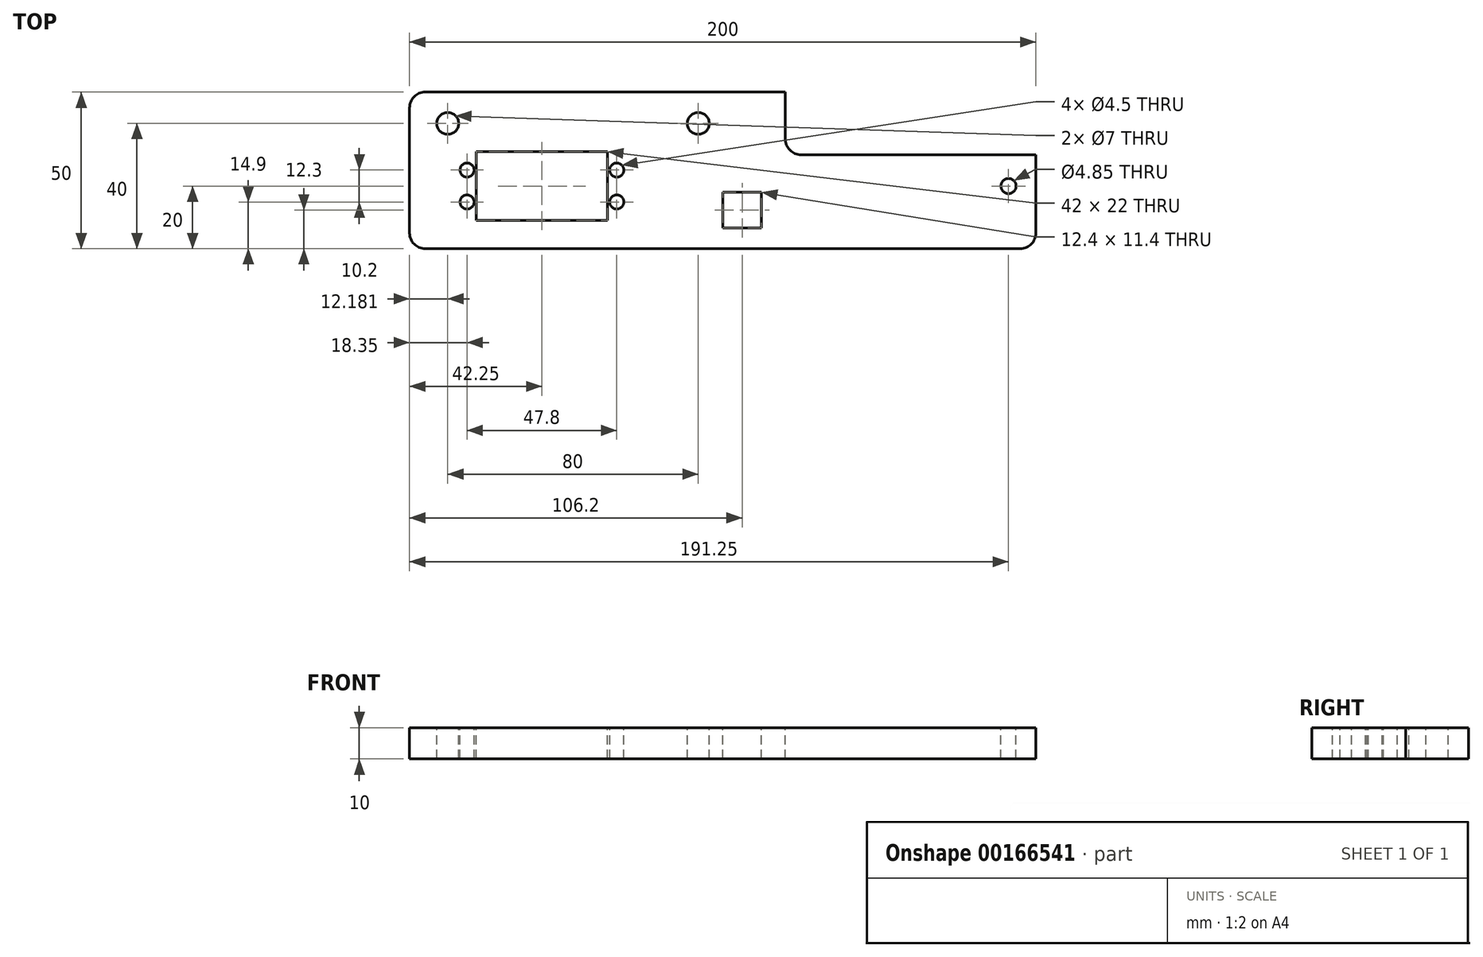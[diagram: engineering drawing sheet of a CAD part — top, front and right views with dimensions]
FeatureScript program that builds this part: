
annotation { "Feature Type Name" : "Feature", "Feature Type Description" : "" }
export const myFeature = defineFeature(function(context is Context, id is Id, definition is map)
    precondition{}
    {
        {
            var Q0;
            Q0=qCreatedBy(makeId("Top.planeOp"),FACE);
            var sketch = newSketch(context, id + "F0", { "sketchPlane" : qUnion([Q0])});
            skLineSegment(sketch, "E0.bottom", {"start": v(100, -25) * mm, "end": v(-100, -25) * mm});
            skLineSegment(sketch, "E0.top", {"start": v(100, 25) * mm, "end": v(-100, 25) * mm});
            skLineSegment(sketch, "E0.left", {"start": v(100, -25) * mm, "end": v(100, 25) * mm});
            skLineSegment(sketch, "E0.right", {"start": v(-100, -25) * mm, "end": v(-100, 25) * mm});
            skPoint(sketch, "E0.middle", {"position": v(0, 0) * mm});
            skSolve(sketch);
        }
        {
            var Q0;
            Q0=makeQuery(id+"F0.imprint","IMPRINT",FACE,{"disambiguationData":[TD([[makeQuery(id+"F0.imprint","IMPRINT",EDGE,{"derivedFrom":sQuery(id+"F0.wireOp",EDGE,"E0.bottom")}),-1.0]])]});
            extrude(context, id + "F1", {"entities" : qUnion([Q0]), "depth" : 10 * mm});
        }
        {
            var Q0;
            Q0=makeQuery(id+"F1.opExtrude","CAP_FACE",FACE,{"disambiguationData":[OSD([sQuery(id+"F0.wireOp",EDGE,"E0.bottom"),sQuery(id+"F0.wireOp",EDGE,"E0.top"),sQuery(id+"F0.wireOp",EDGE,"E0.left"),sQuery(id+"F0.wireOp",EDGE,"E0.right")])],"isStart":false});
            var sketch = newSketch(context, id + "F2", { "sketchPlane" : qUnion([Q0])});
            skLineSegment(sketch, "E1.bottom", {"start": v(-78.75, -16) * mm, "end": v(-36.75, -16) * mm});
            skLineSegment(sketch, "E1.top", {"start": v(-78.75, 6) * mm, "end": v(-36.75, 6) * mm});
            skLineSegment(sketch, "E1.left", {"start": v(-78.75, -16) * mm, "end": v(-78.75, 6) * mm});
            skLineSegment(sketch, "E1.right", {"start": v(-36.75, -16) * mm, "end": v(-36.75, 6) * mm});
            skPoint(sketch, "E1.middle", {"position": v(-57.75, -5) * mm});
            skSolve(sketch);
        }
        {
            var Q0;
            Q0=makeQuery(id+"F2.imprint","IMPRINT",FACE,{"disambiguationData":[TD([[makeQuery(id+"F2.imprint","IMPRINT",EDGE,{"derivedFrom":sQuery(id+"F2.wireOp",EDGE,"E1.bottom")}),1.0]])]});
            extrude(context, id + "F3", {"entities" : qUnion([Q0]), "operationType" : NewBodyOperationType.REMOVE, "endBound" : BoundingType.THROUGH_ALL, "oppositeDirection" : true, "depth" : 25 * mm});
        }
        {
            var Q0;
            Q0=makeQuery(id+"F1.opExtrude","CAP_FACE",FACE,{"disambiguationData":[OSD([sQuery(id+"F0.wireOp",EDGE,"E0.bottom"),sQuery(id+"F0.wireOp",EDGE,"E0.top"),sQuery(id+"F0.wireOp",EDGE,"E0.left"),sQuery(id+"F0.wireOp",EDGE,"E0.right")])],"isStart":false});
            var sketch = newSketch(context, id + "F4", { "sketchPlane" : qUnion([Q0])});
            skLineSegment(sketch, "E2.bottom", {"start": v(-81.65, 0.1) * mm, "end": v(-33.85, 0.1) * mm});
            skLineSegment(sketch, "E2.top", {"start": v(-81.65, -10.1) * mm, "end": v(-33.85, -10.1) * mm});
            skLineSegment(sketch, "E2.left", {"start": v(-81.65, 0.1) * mm, "end": v(-81.65, -10.1) * mm});
            skLineSegment(sketch, "E2.right", {"start": v(-33.85, 0.1) * mm, "end": v(-33.85, -10.1) * mm});
            skPoint(sketch, "E2.middle", {"position": v(-57.75, -5) * mm});
            skPoint(sketch, "E2.middle.positionSnap0", {"position": v(-78.75, -5) * mm});
            skPoint(sketch, "E2.middle.positionSnap1", {"position": v(-57.75, -16) * mm});
            skPoint(sketch, "E2.centerSnap0", {"position": v(-78.75, -5) * mm});
            skPoint(sketch, "E2.centerSnap1", {"position": v(-57.75, -16) * mm});
            skCircle(sketch, "E3", {"center": v(-81.65, 0.1) * mm, "radius": 2.25 * mm});
            skCircle(sketch, "E4", {"center": v(-81.65, -10.1) * mm, "radius": 2.25 * mm});
            skCircle(sketch, "E5", {"center": v(-33.85, 0.1) * mm, "radius": 2.25 * mm});
            skCircle(sketch, "E6", {"center": v(-33.85, -10.1) * mm, "radius": 2.25 * mm});
            skSolve(sketch);
        }
        {
            var Q0;
            {var subQ0=sQuery(id+"F4.wireOp",EDGE,"E2.left");var subQ1=sQuery(id+"F4.wireOp",EDGE,"E2.bottom");var subQ2=makeQuery(id+"F4.imprint","INTERSECT",VERTEX,{"derivedFrom":[subQ1,subQ0]});Q0=makeQuery(id+"F4.imprint","IMPRINT",FACE,{"disambiguationData":[TD([[makeQuery(id+"F4.imprint","IMPRINT",EDGE,{"disambiguationData":[TD([[subQ2,-1.0]])],"derivedFrom":subQ1}),1.0]])]});}
            var Q1;
            {var subQ0=sQuery(id+"F4.wireOp",EDGE,"E2.left");var subQ1=sQuery(id+"F4.wireOp",EDGE,"E2.bottom");var subQ2=makeQuery(id+"F4.imprint","INTERSECT",VERTEX,{"derivedFrom":[subQ1,subQ0]});Q1=makeQuery(id+"F4.imprint","IMPRINT",FACE,{"disambiguationData":[TD([[makeQuery(id+"F4.imprint","IMPRINT",EDGE,{"disambiguationData":[TD([[subQ2,-1.0]])],"derivedFrom":subQ1}),-1.0]])]});}
            var Q2;
            {var subQ0=sQuery(id+"F4.wireOp",EDGE,"E2.left");var subQ1=sQuery(id+"F4.wireOp",EDGE,"E2.top");var subQ2=makeQuery(id+"F4.imprint","INTERSECT",VERTEX,{"derivedFrom":[subQ1,subQ0]});Q2=makeQuery(id+"F4.imprint","IMPRINT",FACE,{"disambiguationData":[TD([[makeQuery(id+"F4.imprint","IMPRINT",EDGE,{"disambiguationData":[TD([[subQ2,-1.0]])],"derivedFrom":subQ1}),-1.0]])]});}
            var Q3;
            {var subQ0=sQuery(id+"F4.wireOp",EDGE,"E2.left");var subQ1=sQuery(id+"F4.wireOp",EDGE,"E2.top");var subQ2=makeQuery(id+"F4.imprint","INTERSECT",VERTEX,{"derivedFrom":[subQ1,subQ0]});Q3=makeQuery(id+"F4.imprint","IMPRINT",FACE,{"disambiguationData":[TD([[makeQuery(id+"F4.imprint","IMPRINT",EDGE,{"disambiguationData":[TD([[subQ2,-1.0]])],"derivedFrom":subQ1}),1.0]])]});}
            var Q4;
            {var subQ0=sQuery(id+"F4.wireOp",EDGE,"E2.right");var subQ1=sQuery(id+"F4.wireOp",EDGE,"E2.bottom");var subQ2=makeQuery(id+"F4.imprint","INTERSECT",VERTEX,{"derivedFrom":[subQ1,subQ0]});Q4=makeQuery(id+"F4.imprint","IMPRINT",FACE,{"disambiguationData":[TD([[makeQuery(id+"F4.imprint","IMPRINT",EDGE,{"disambiguationData":[TD([[subQ2,1.0]])],"derivedFrom":subQ1}),-1.0]])]});}
            var Q5;
            {var subQ0=sQuery(id+"F4.wireOp",EDGE,"E2.right");var subQ1=sQuery(id+"F4.wireOp",EDGE,"E2.bottom");var subQ2=makeQuery(id+"F4.imprint","INTERSECT",VERTEX,{"derivedFrom":[subQ1,subQ0]});Q5=makeQuery(id+"F4.imprint","IMPRINT",FACE,{"disambiguationData":[TD([[makeQuery(id+"F4.imprint","IMPRINT",EDGE,{"disambiguationData":[TD([[subQ2,1.0]])],"derivedFrom":subQ1}),1.0]])]});}
            var Q6;
            {var subQ0=sQuery(id+"F4.wireOp",EDGE,"E2.right");var subQ1=sQuery(id+"F4.wireOp",EDGE,"E2.top");var subQ2=makeQuery(id+"F4.imprint","INTERSECT",VERTEX,{"derivedFrom":[subQ1,subQ0]});Q6=makeQuery(id+"F4.imprint","IMPRINT",FACE,{"disambiguationData":[TD([[makeQuery(id+"F4.imprint","IMPRINT",EDGE,{"disambiguationData":[TD([[subQ2,1.0]])],"derivedFrom":subQ1}),1.0]])]});}
            var Q7;
            {var subQ0=sQuery(id+"F4.wireOp",EDGE,"E2.right");var subQ1=sQuery(id+"F4.wireOp",EDGE,"E2.top");var subQ2=makeQuery(id+"F4.imprint","INTERSECT",VERTEX,{"derivedFrom":[subQ1,subQ0]});Q7=makeQuery(id+"F4.imprint","IMPRINT",FACE,{"disambiguationData":[TD([[makeQuery(id+"F4.imprint","IMPRINT",EDGE,{"disambiguationData":[TD([[subQ2,1.0]])],"derivedFrom":subQ1}),-1.0]])]});}
            extrude(context, id + "F5", {"entities" : qUnion([Q0, Q1, Q2, Q3, Q4, Q5, Q6, Q7]), "operationType" : NewBodyOperationType.REMOVE, "endBound" : BoundingType.THROUGH_ALL, "oppositeDirection" : true, "depth" : 25 * mm});
        }
        {
            var Q0;
            Q0=makeQuery(id+"F1.opExtrude","CAP_FACE",FACE,{"disambiguationData":[OSD([sQuery(id+"F0.wireOp",EDGE,"E0.bottom"),sQuery(id+"F0.wireOp",EDGE,"E0.top"),sQuery(id+"F0.wireOp",EDGE,"E0.left"),sQuery(id+"F0.wireOp",EDGE,"E0.right")])],"isStart":false});
            var sketch = newSketch(context, id + "F6", { "sketchPlane" : qUnion([Q0])});
            skLineSegment(sketch, "E7.bottom", {"start": v(-87.82, 15) * mm, "end": v(-7.82, 15) * mm});
            skLineSegment(sketch, "E7.top", {"start": v(-87.82, -25) * mm, "end": v(-7.82, -25) * mm});
            skLineSegment(sketch, "E7.left", {"start": v(-87.82, 15) * mm, "end": v(-87.82, -25) * mm});
            skLineSegment(sketch, "E7.right", {"start": v(-7.82, 15) * mm, "end": v(-7.82, -25) * mm});
            skCircle(sketch, "E8", {"center": v(-87.82, 15) * mm, "radius": 3.5 * mm});
            skCircle(sketch, "E9", {"center": v(-7.82, 15) * mm, "radius": 3.5 * mm});
            skSolve(sketch);
        }
        {
            var Q0;
            {var subQ0=sQuery(id+"F6.wireOp",EDGE,"E7.left");var subQ1=sQuery(id+"F6.wireOp",EDGE,"E7.bottom");var subQ2=makeQuery(id+"F6.imprint","INTERSECT",VERTEX,{"derivedFrom":[subQ1,subQ0]});Q0=makeQuery(id+"F6.imprint","IMPRINT",FACE,{"disambiguationData":[TD([[makeQuery(id+"F6.imprint","IMPRINT",EDGE,{"disambiguationData":[TD([[subQ2,-1.0]])],"derivedFrom":subQ1}),1.0]])]});}
            var Q1;
            {var subQ0=sQuery(id+"F6.wireOp",EDGE,"E7.left");var subQ1=sQuery(id+"F6.wireOp",EDGE,"E7.bottom");var subQ2=makeQuery(id+"F6.imprint","INTERSECT",VERTEX,{"derivedFrom":[subQ1,subQ0]});Q1=makeQuery(id+"F6.imprint","IMPRINT",FACE,{"disambiguationData":[TD([[makeQuery(id+"F6.imprint","IMPRINT",EDGE,{"disambiguationData":[TD([[subQ2,-1.0]])],"derivedFrom":subQ1}),-1.0]])]});}
            var Q2;
            {var subQ0=sQuery(id+"F6.wireOp",EDGE,"E7.right");var subQ1=sQuery(id+"F6.wireOp",EDGE,"E7.bottom");var subQ2=makeQuery(id+"F6.imprint","INTERSECT",VERTEX,{"derivedFrom":[subQ1,subQ0]});Q2=makeQuery(id+"F6.imprint","IMPRINT",FACE,{"disambiguationData":[TD([[makeQuery(id+"F6.imprint","IMPRINT",EDGE,{"disambiguationData":[TD([[subQ2,1.0]])],"derivedFrom":subQ1}),-1.0]])]});}
            var Q3;
            {var subQ0=sQuery(id+"F6.wireOp",EDGE,"E7.right");var subQ1=sQuery(id+"F6.wireOp",EDGE,"E7.bottom");var subQ2=makeQuery(id+"F6.imprint","INTERSECT",VERTEX,{"derivedFrom":[subQ1,subQ0]});Q3=makeQuery(id+"F6.imprint","IMPRINT",FACE,{"disambiguationData":[TD([[makeQuery(id+"F6.imprint","IMPRINT",EDGE,{"disambiguationData":[TD([[subQ2,1.0]])],"derivedFrom":subQ1}),1.0]])]});}
            extrude(context, id + "F7", {"entities" : qUnion([Q0, Q1, Q2, Q3]), "operationType" : NewBodyOperationType.REMOVE, "endBound" : BoundingType.THROUGH_ALL, "oppositeDirection" : true, "depth" : 25 * mm});
        }
        {
            var Q0;
            Q0=makeQuery(id+"F1.opExtrude","SWEPT_EDGE",EDGE,{"disambiguationData":[OSD([sQuery(id+"F0.wireOp",EDGE,"E0.top"),sQuery(id+"F0.wireOp",EDGE,"E0.right")])]});
            var Q1;
            Q1=makeQuery(id+"F1.opExtrude","SWEPT_EDGE",EDGE,{"disambiguationData":[OSD([sQuery(id+"F0.wireOp",EDGE,"E0.bottom"),sQuery(id+"F0.wireOp",EDGE,"E0.right")])]});
            var Q2;
            Q2=makeQuery(id+"F1.opExtrude","SWEPT_EDGE",EDGE,{"disambiguationData":[OSD([sQuery(id+"F0.wireOp",EDGE,"E0.top"),sQuery(id+"F0.wireOp",EDGE,"E0.left")])]});
            var Q3;
            Q3=makeQuery(id+"F1.opExtrude","SWEPT_EDGE",EDGE,{"disambiguationData":[OSD([sQuery(id+"F0.wireOp",EDGE,"E0.bottom"),sQuery(id+"F0.wireOp",EDGE,"E0.left")])]});
            fillet(context, id + "F8", {"entities" : qUnion([Q0, Q1, Q2, Q3]), "radius" : 5 * mm, "tangentPropagation" : true, "allowEdgeOverflow" : false});
        }
        {
            var Q0;
            Q0=makeQuery(id+"F1.opExtrude","CAP_FACE",FACE,{"disambiguationData":[OSD([sQuery(id+"F0.wireOp",EDGE,"E0.bottom"),sQuery(id+"F0.wireOp",EDGE,"E0.top"),sQuery(id+"F0.wireOp",EDGE,"E0.left"),sQuery(id+"F0.wireOp",EDGE,"E0.right")])],"isStart":false});
            var sketch = newSketch(context, id + "F9", { "sketchPlane" : qUnion([Q0])});
            skLineSegment(sketch, "E10.bottom", {"start": v(0, -7) * mm, "end": v(12.4, -7) * mm});
            skLineSegment(sketch, "E10.top", {"start": v(0, -18.4) * mm, "end": v(12.4, -18.4) * mm});
            skLineSegment(sketch, "E10.left", {"start": v(0, -7) * mm, "end": v(0, -18.4) * mm});
            skLineSegment(sketch, "E10.right", {"start": v(12.4, -7) * mm, "end": v(12.4, -18.4) * mm});
            skSolve(sketch);
        }
        {
            var Q0;
            Q0=makeQuery(id+"F1.opExtrude","CAP_FACE",FACE,{"disambiguationData":[OSD([sQuery(id+"F0.wireOp",EDGE,"E0.bottom"),sQuery(id+"F0.wireOp",EDGE,"E0.top"),sQuery(id+"F0.wireOp",EDGE,"E0.left"),sQuery(id+"F0.wireOp",EDGE,"E0.right")])],"isStart":false});
            var sketch = newSketch(context, id + "F10", { "sketchPlane" : qUnion([Q0])});
            skLineSegment(sketch, "E11.bottom", {"start": v(-78.75, -5) * mm, "end": v(91.25, -5) * mm});
            skLineSegment(sketch, "E11.top", {"start": v(-78.75, -25) * mm, "end": v(91.25, -25) * mm});
            skLineSegment(sketch, "E11.left", {"start": v(-78.75, -5) * mm, "end": v(-78.75, -25) * mm});
            skLineSegment(sketch, "E11.right", {"start": v(91.25, -5) * mm, "end": v(91.25, -25) * mm});
            skCircle(sketch, "E12", {"center": v(91.25, -5) * mm, "radius": 2.43 * mm});
            skSolve(sketch);
        }
        {
            var Q0;
            {var subQ0=sQuery(id+"F10.wireOp",EDGE,"E11.right");Q0=makeQuery(id+"F10.imprint","IMPRINT",FACE,{"disambiguationData":[TD([[makeQuery(id+"F10.imprint","IMPRINT",EDGE,{"derivedFrom":subQ0}),1.0]])]});}
            var sketch = newSketch(context, id + "F11", { "sketchPlane" : qUnion([Q0])});
            skLineSegment(sketch, "E13.bottom", {"start": v(100, 5) * mm, "end": v(20, 5) * mm});
            skLineSegment(sketch, "E13.top", {"start": v(100, 25) * mm, "end": v(20, 25) * mm});
            skLineSegment(sketch, "E13.left", {"start": v(100, 5) * mm, "end": v(100, 25) * mm});
            skLineSegment(sketch, "E13.right", {"start": v(20, 5) * mm, "end": v(20, 25) * mm});
            skSolve(sketch);
        }
        {
            var Q0;
            Q0=qSketchRegion(id+"F11",true);
            var Q1;
            {var subQ0=sQuery(id+"F10.wireOp",EDGE,"E11.right");var subQ1=sQuery(id+"F10.wireOp",EDGE,"E11.bottom");var subQ2=makeQuery(id+"F10.imprint","INTERSECT",VERTEX,{"derivedFrom":[subQ1,subQ0]});Q1=makeQuery(id+"F10.imprint","IMPRINT",FACE,{"disambiguationData":[TD([[makeQuery(id+"F10.imprint","IMPRINT",EDGE,{"disambiguationData":[TD([[subQ2,1.0]])],"derivedFrom":subQ1}),1.0]])]});}
            var Q2;
            {var subQ0=sQuery(id+"F10.wireOp",EDGE,"E11.right");var subQ1=sQuery(id+"F10.wireOp",EDGE,"E11.bottom");var subQ2=makeQuery(id+"F10.imprint","INTERSECT",VERTEX,{"derivedFrom":[subQ1,subQ0]});Q2=makeQuery(id+"F10.imprint","IMPRINT",FACE,{"disambiguationData":[TD([[makeQuery(id+"F10.imprint","IMPRINT",EDGE,{"disambiguationData":[TD([[subQ2,1.0]])],"derivedFrom":subQ1}),-1.0]])]});}
            var Q3;
            Q3=makeQuery(id+"F9.imprint","IMPRINT",FACE,{"disambiguationData":[TD([[makeQuery(id+"F9.imprint","IMPRINT",EDGE,{"derivedFrom":sQuery(id+"F9.wireOp",EDGE,"E10.bottom")}),-1.0]])]});
            extrude(context, id + "F12", {"entities" : qUnion([Q0, Q1, Q2, Q3]), "operationType" : NewBodyOperationType.REMOVE, "endBound" : BoundingType.THROUGH_ALL, "oppositeDirection" : true, "depth" : 25 * mm});
        }
        {
            var Q0;
            Q0=makeQuery(id+"F12.boolean.opBoolean","COPY",EDGE,{"derivedFrom":makeQuery(id+"F12.opExtrude","SWEPT_EDGE",EDGE,{"disambiguationData":[OSD([sQuery(id+"F0.wireOp",EDGE,"E0.top"),sQuery(id+"F11.wireOp",EDGE,"E13.top"),sQuery(id+"F11.wireOp",EDGE,"E13.right")])]})});
            var Q1;
            Q1=makeQuery(id+"F12.boolean.opBoolean","COPY",EDGE,{"derivedFrom":makeQuery(id+"F12.opExtrude","SWEPT_EDGE",EDGE,{"disambiguationData":[OSD([sQuery(id+"F11.wireOp",EDGE,"E13.bottom"),sQuery(id+"F11.wireOp",EDGE,"E13.right")])]})});
            var Q2;
            Q2=makeQuery(id+"F12.boolean.opBoolean","COPY",EDGE,{"derivedFrom":makeQuery(id+"F12.opExtrude","SWEPT_EDGE",EDGE,{"disambiguationData":[OSD([sQuery(id+"F0.wireOp",EDGE,"E0.left"),sQuery(id+"F11.wireOp",EDGE,"E13.bottom"),sQuery(id+"F11.wireOp",EDGE,"E13.left")])]})});
            fillet(context, id + "F13", {"entities" : qUnion([Q0, Q1, Q2]), "radius" : 5 * mm, "tangentPropagation" : true, "allowEdgeOverflow" : false});
        }
    });
